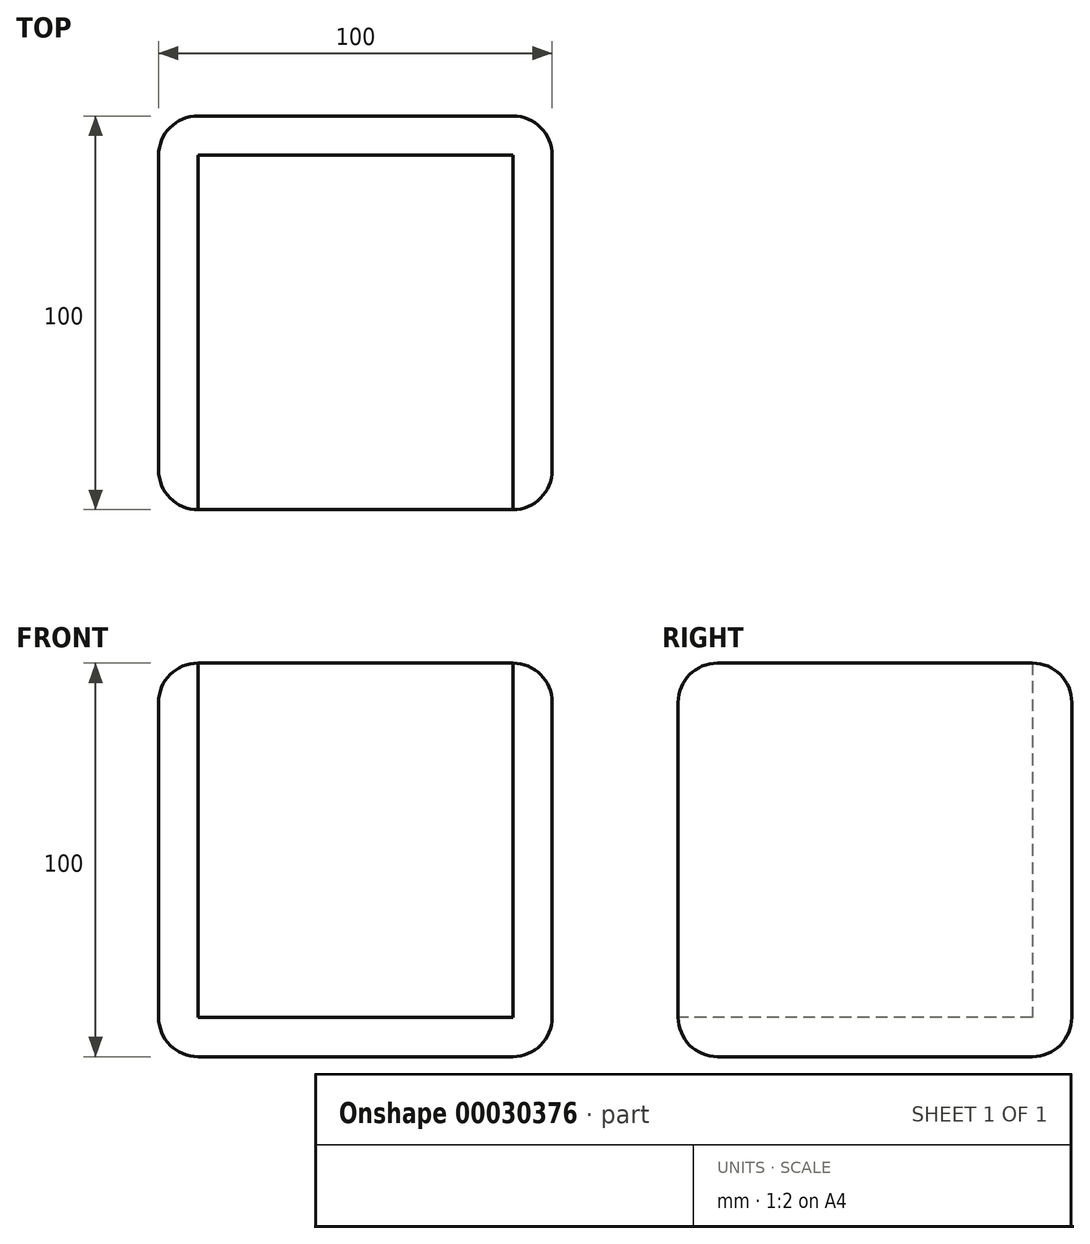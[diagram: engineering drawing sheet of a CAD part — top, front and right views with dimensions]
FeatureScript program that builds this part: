
annotation { "Feature Type Name" : "Feature", "Feature Type Description" : "" }
export const myFeature = defineFeature(function(context is Context, id is Id, definition is map)
    precondition{}
    {
        {
            var Q0;
            Q0=qCreatedBy(makeId("Front.planeOp"),FACE);
            var sketch = newSketch(context, id + "F0", { "sketchPlane" : qUnion([Q0])});
            skLineSegment(sketch, "E0.bottom", {"start": v(-50.52, -49.37) * mm, "end": v(49.48, -49.37) * mm});
            skLineSegment(sketch, "E0.top", {"start": v(-50.52, 50.63) * mm, "end": v(49.48, 50.63) * mm});
            skLineSegment(sketch, "E0.left", {"start": v(-50.52, -49.37) * mm, "end": v(-50.52, 50.63) * mm});
            skLineSegment(sketch, "E0.right", {"start": v(49.48, -49.37) * mm, "end": v(49.48, 50.63) * mm});
            skSolve(sketch);
        }
        {
            var Q0;
            Q0=makeQuery(id+"F0.imprint","IMPRINT",FACE,{"disambiguationData":[TD([[makeQuery(id+"F0.imprint","IMPRINT",EDGE,{"derivedFrom":sQuery(id+"F0.wireOp",EDGE,"E0.bottom")}),1.0]])]});
            extrude(context, id + "F1", {"entities" : qUnion([Q0]), "endBound" : BoundingType.SYMMETRIC, "depth" : 100 * mm});
        }
        {
            var Q0;
            Q0=makeQuery(id+"F1.opExtrude","CAP_EDGE",EDGE,{"disambiguationData":[OSD([sQuery(id+"F0.wireOp",EDGE,"E0.top")])],"isStart":false});
            var Q1;
            Q1=makeQuery(id+"F1.opExtrude","CAP_EDGE",EDGE,{"disambiguationData":[OSD([sQuery(id+"F0.wireOp",EDGE,"E0.left")])],"isStart":false});
            var Q2;
            Q2=makeQuery(id+"F1.opExtrude","CAP_EDGE",EDGE,{"disambiguationData":[OSD([sQuery(id+"F0.wireOp",EDGE,"E0.bottom")])],"isStart":false});
            var Q3;
            Q3=makeQuery(id+"F1.opExtrude","CAP_EDGE",EDGE,{"disambiguationData":[OSD([sQuery(id+"F0.wireOp",EDGE,"E0.right")])],"isStart":false});
            var Q4;
            Q4=makeQuery(id+"F1.opExtrude","SWEPT_EDGE",EDGE,{"disambiguationData":[OSD([sQuery(id+"F0.wireOp",EDGE,"E0.top"),sQuery(id+"F0.wireOp",EDGE,"E0.left")])]});
            var Q5;
            Q5=makeQuery(id+"F1.opExtrude","CAP_EDGE",EDGE,{"disambiguationData":[OSD([sQuery(id+"F0.wireOp",EDGE,"E0.left")])],"isStart":true});
            var Q6;
            Q6=makeQuery(id+"F1.opExtrude","SWEPT_EDGE",EDGE,{"disambiguationData":[OSD([sQuery(id+"F0.wireOp",EDGE,"E0.bottom"),sQuery(id+"F0.wireOp",EDGE,"E0.left")])]});
            var Q7;
            Q7=makeQuery(id+"F1.opExtrude","SWEPT_EDGE",EDGE,{"disambiguationData":[OSD([sQuery(id+"F0.wireOp",EDGE,"E0.bottom"),sQuery(id+"F0.wireOp",EDGE,"E0.right")])]});
            var Q8;
            Q8=makeQuery(id+"F1.opExtrude","CAP_EDGE",EDGE,{"disambiguationData":[OSD([sQuery(id+"F0.wireOp",EDGE,"E0.bottom")])],"isStart":true});
            var Q9;
            Q9=makeQuery(id+"F1.opExtrude","SWEPT_EDGE",EDGE,{"disambiguationData":[OSD([sQuery(id+"F0.wireOp",EDGE,"E0.top"),sQuery(id+"F0.wireOp",EDGE,"E0.right")])]});
            var Q10;
            Q10=makeQuery(id+"F1.opExtrude","CAP_EDGE",EDGE,{"disambiguationData":[OSD([sQuery(id+"F0.wireOp",EDGE,"E0.top")])],"isStart":true});
            var Q11;
            Q11=makeQuery(id+"F1.opExtrude","CAP_EDGE",EDGE,{"disambiguationData":[OSD([sQuery(id+"F0.wireOp",EDGE,"E0.right")])],"isStart":true});
            fillet(context, id + "F2", {"entities" : qUnion([Q0, Q1, Q2, Q3, Q4, Q5, Q6, Q7, Q8, Q9, Q10, Q11]), "radius" : 10 * mm, "tangentPropagation" : true, "allowEdgeOverflow" : false});
        }
        {
            var Q0;
            {var subQ0=sQuery(id+"F0.wireOp",EDGE,"E0.top");Q0=makeQuery(id+"F2.opFillet","BLEND_FACE",FACE,{"disambiguationData":[OSD([subQ0]),TDD([makeQuery(id+"F1.opExtrude","CAP_EDGE",EDGE,{"disambiguationData":[OSD([subQ0])],"isStart":false})])]});}
            var Q1;
            Q1=makeQuery(id+"F1.opExtrude","CAP_FACE",FACE,{"disambiguationData":[OSD([sQuery(id+"F0.wireOp",EDGE,"E0.bottom"),sQuery(id+"F0.wireOp",EDGE,"E0.top"),sQuery(id+"F0.wireOp",EDGE,"E0.left"),sQuery(id+"F0.wireOp",EDGE,"E0.right")])],"isStart":false});
            var Q2;
            Q2=makeQuery(id+"F1.opExtrude","SWEPT_FACE",FACE,{"disambiguationData":[OSD([sQuery(id+"F0.wireOp",EDGE,"E0.top")])]});
            shell(context, id + "F3", {"entities" : qUnion([Q0, Q1, Q2]), "thickness" : 10 * mm});
        }
    });
